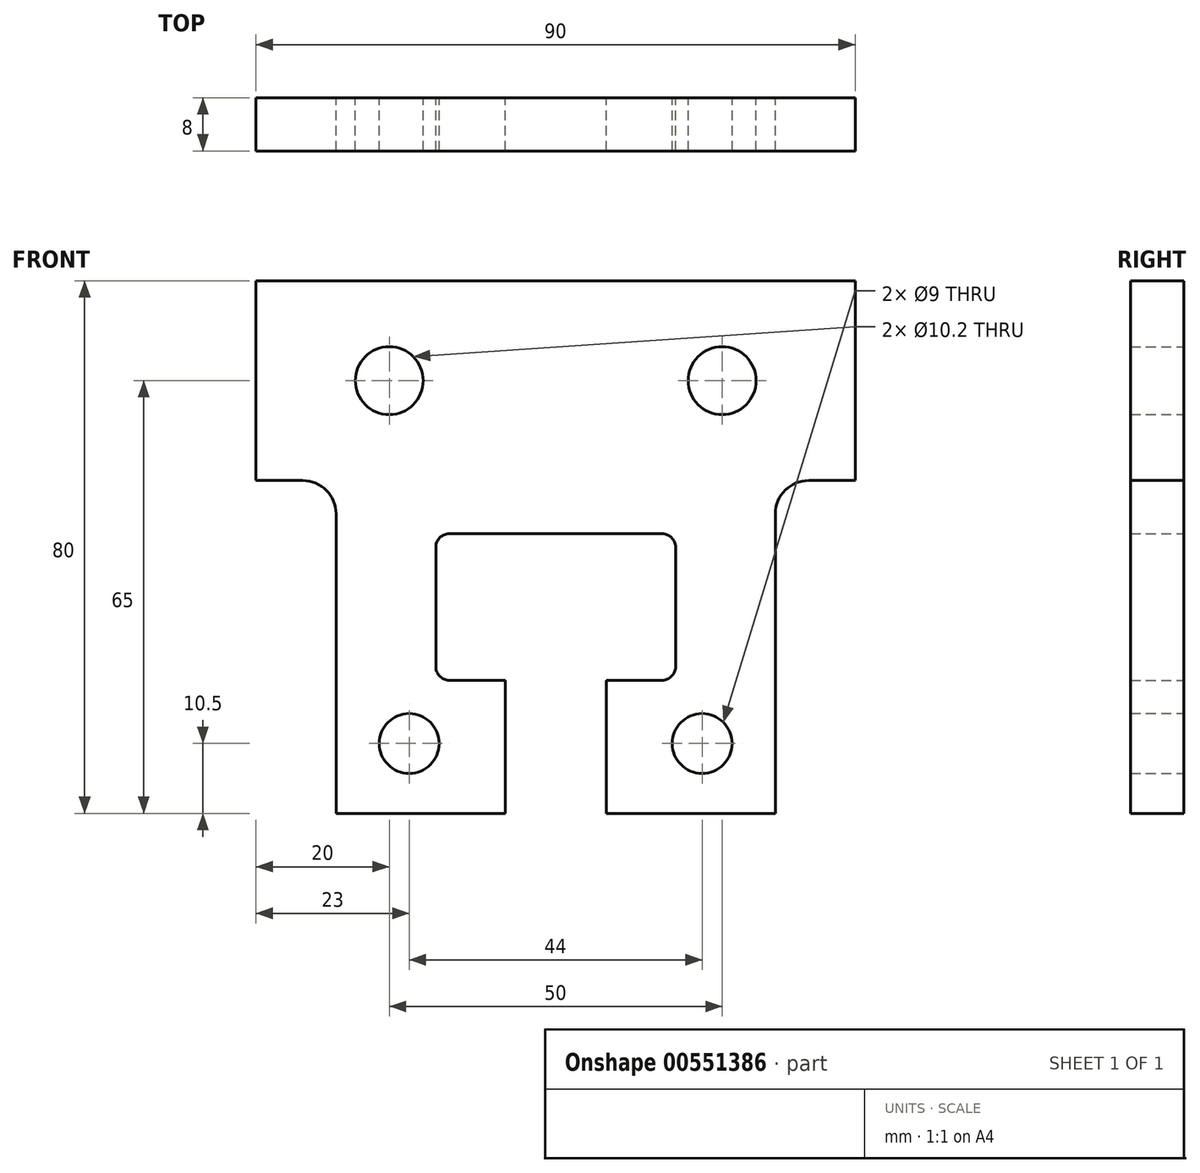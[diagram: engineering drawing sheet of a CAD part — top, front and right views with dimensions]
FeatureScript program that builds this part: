
annotation { "Feature Type Name" : "Feature", "Feature Type Description" : "" }
export const myFeature = defineFeature(function(context is Context, id is Id, definition is map)
    precondition{}
    {
        {
            var Q0;
            Q0=qCreatedBy(makeId("Front.planeOp"),FACE);
            var sketch = newSketch(context, id + "F0", { "sketchPlane" : qUnion([Q0])});
            skLineSegment(sketch, "E0", {"start": v(0, 0) * mm, "end": v(-45, 0) * mm});
            skLineSegment(sketch, "E1", {"start": v(-45, 0) * mm, "end": v(-45, -30) * mm});
            skLineSegment(sketch, "E2", {"start": v(-45, -30) * mm, "end": v(-38, -30) * mm});
            skLineSegment(sketch, "E3", {"start": v(-33, -35) * mm, "end": v(-33, -80) * mm});
            skLineSegment(sketch, "E4", {"start": v(-33, -80) * mm, "end": v(-7.6, -80) * mm});
            skLineSegment(sketch, "E5", {"start": v(-7.6, -80) * mm, "end": v(-7.6, -60) * mm});
            skLineSegment(sketch, "E6", {"start": v(-7.6, -60) * mm, "end": v(-16, -60) * mm});
            skLineSegment(sketch, "E7", {"start": v(-18, -58) * mm, "end": v(-18, -40) * mm});
            skLineSegment(sketch, "E8", {"start": v(-16, -38) * mm, "end": v(0, -38) * mm});
            skLineSegment(sketch, "E9", {"start": v(0, -38) * mm, "end": v(0, 0) * mm});
            skCircle(sketch, "E10", {"center": v(-22, -69.5) * mm, "radius": 4.5 * mm});
            skCircle(sketch, "E11", {"center": v(-25, -15) * mm, "radius": 5.1 * mm});
            skPoint(sketch, "E12.visualSharp", {"position": v(-33, -30) * mm});
            skArc(sketch, "E12.filletArc", {"start": v(-33, -35) * mm, "mid": v(-34.46, -31.46) * mm, "end": v(-38, -30) * mm});
            skPoint(sketch, "E13.visualSharp", {"position": v(-18, -38) * mm});
            skArc(sketch, "E13.filletArc", {"start": v(-16, -38) * mm, "mid": v(-17.41, -38.59) * mm, "end": v(-18, -40) * mm});
            skPoint(sketch, "E14.visualSharp", {"position": v(-18, -60) * mm});
            skArc(sketch, "E14.filletArc", {"start": v(-18, -58) * mm, "mid": v(-17.41, -59.41) * mm, "end": v(-16, -60) * mm});
            skSolve(sketch);
        }
        {
            var Q0;
            Q0=makeQuery(id+"F0.imprint","IMPRINT",FACE,{"disambiguationData":[TD([[makeQuery(id+"F0.imprint","IMPRINT",EDGE,{"derivedFrom":sQuery(id+"F0.wireOp",EDGE,"E0")}),1.0]])]});
            extrude(context, id + "F1", {"entities" : qUnion([Q0]), "depth" : 8 * mm, "offsetDistance" : 25 * mm});
        }
        {
            var Q0;
            Q0=makeQuery(id+"F1.opExtrude","SWEPT_BODY",BODY,{"disambiguationData":[OSD([sQuery(id+"F0.wireOp",EDGE,"E0"),sQuery(id+"F0.wireOp",EDGE,"E1"),sQuery(id+"F0.wireOp",EDGE,"E2"),sQuery(id+"F0.wireOp",EDGE,"E3"),sQuery(id+"F0.wireOp",EDGE,"E4"),sQuery(id+"F0.wireOp",EDGE,"E5"),sQuery(id+"F0.wireOp",EDGE,"E6"),sQuery(id+"F0.wireOp",EDGE,"E7"),sQuery(id+"F0.wireOp",EDGE,"E8"),sQuery(id+"F0.wireOp",EDGE,"E9"),sQuery(id+"F0.wireOp",EDGE,"E10"),sQuery(id+"F0.wireOp",EDGE,"E11"),sQuery(id+"F0.wireOp",EDGE,"E12.filletArc"),sQuery(id+"F0.wireOp",EDGE,"E13.filletArc"),sQuery(id+"F0.wireOp",EDGE,"E14.filletArc")])]});
            var Q1;
            Q1=makeQuery(id+"F1.opExtrude","SWEPT_FACE",FACE,{"disambiguationData":[OSD([sQuery(id+"F0.wireOp",EDGE,"E9")])]});
            mirror(context, id + "F2", {"operationType" : NewBodyOperationType.ADD, "entities" : qUnion([Q0]), "mirrorPlane" : qUnion([Q1])});
        }
    });
